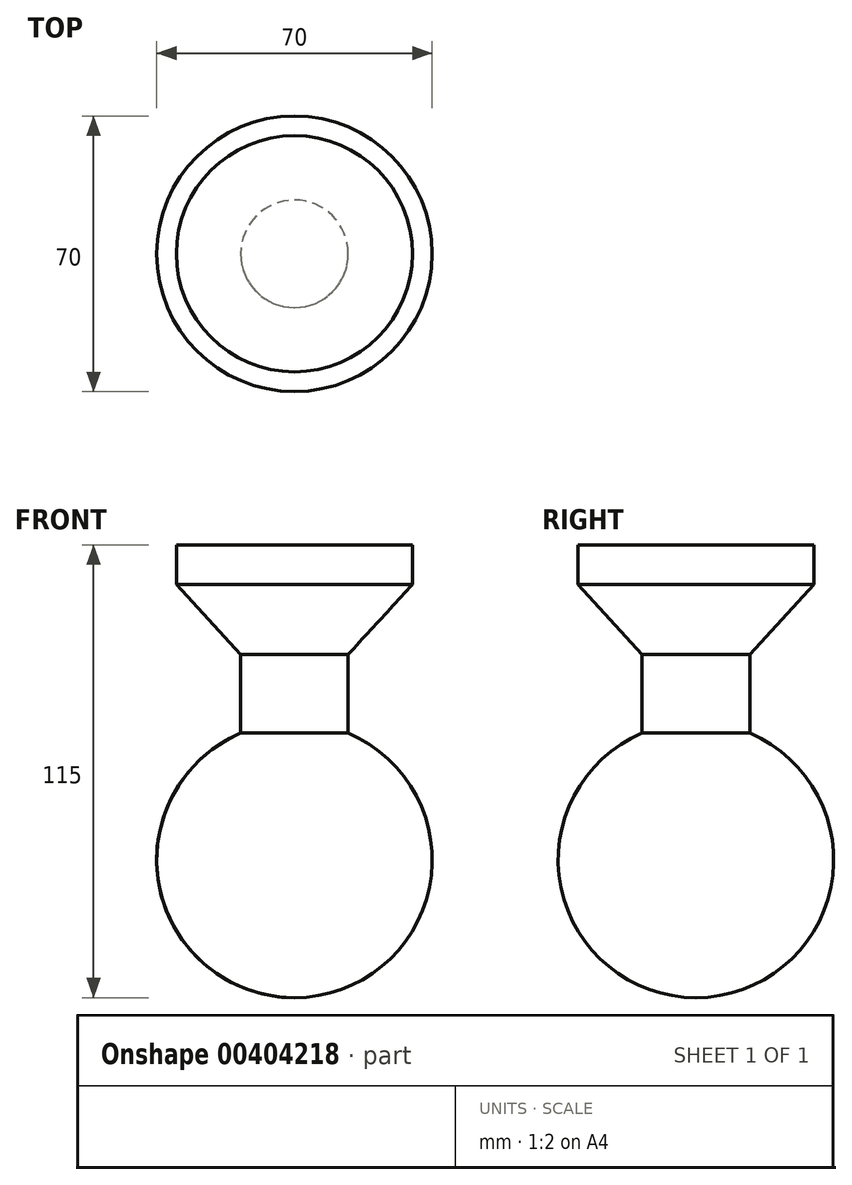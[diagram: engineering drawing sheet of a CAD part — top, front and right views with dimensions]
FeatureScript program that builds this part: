
annotation { "Feature Type Name" : "Feature", "Feature Type Description" : "" }
export const myFeature = defineFeature(function(context is Context, id is Id, definition is map)
    precondition{}
    {
        {
            var Q0;
            Q0=qCreatedBy(makeId("Front.planeOp"),FACE);
            var sketch = newSketch(context, id + "F0", { "sketchPlane" : qUnion([Q0])});
            skArc(sketch, "E0", {"start": v(0, -35) * mm, "mid": v(34.3, -6.97) * mm, "end": v(13.66, 32.22) * mm});
            skLineSegment(sketch, "E1", {"start": v(13.66, 32.22) * mm, "end": v(13.66, 52.22) * mm});
            skLineSegment(sketch, "E2", {"start": v(13.66, 52.22) * mm, "end": v(30, 70) * mm});
            skLineSegment(sketch, "E3", {"start": v(30, 70) * mm, "end": v(30, 80) * mm});
            skLineSegment(sketch, "E4", {"start": v(30, 80) * mm, "end": v(0, 80) * mm});
            skLineSegment(sketch, "E5", {"start": v(0, 80) * mm, "end": v(0, 35) * mm});
            skLineSegment(sketch, "E6", {"start": v(0, 35) * mm, "end": v(0, -35) * mm});
            skSolve(sketch);
        }
        {
            var Q0;
            Q0=makeQuery(id+"F0.imprint","IMPRINT",FACE,{"disambiguationData":[TD([[makeQuery(id+"F0.imprint","IMPRINT",EDGE,{"derivedFrom":sQuery(id+"F0.wireOp",EDGE,"E0")}),1.0]])]});
            var Q1;
            Q1=sQuery(id+"F0.wireOp",EDGE,"E6");
            revolve(context, id + "F1", {"entities" : qUnion([Q0]), "axis" : qUnion([Q1]), "revolveType" : RevolveType.FULL});
        }
    });
